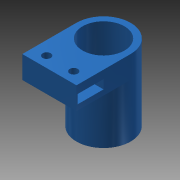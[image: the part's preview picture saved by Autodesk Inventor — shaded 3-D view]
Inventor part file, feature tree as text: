
AUTODESK INVENTOR PART (.ipt)
format: ipt  version: 2013 (Build 170138000, 138)  size: 145,920 bytes
history: native  units: mm
features: extrude x5, sketch x5, plane x2, projected_geometry x1
ambient origin geometry x8: Origin, YZ Plane, XZ Plane, XY Plane, X Axis, Y Axis, Z Axis, Center Point
bodies: Solid1 (feature_tree)
feature tree (13):
  extrude  "Extrusion1"  Depth=30.0mm
  extrude  "Extrusion2"  Depth=15.5mm
  sketch  "Sketch6"  dims[d9=10.0mm d10=5.0mm d11=5.0mm d12=25.0mm d13=0.0mm d15=2.0mm d16=0.0mm d18=3.0mm d19=0.0mm d20=10.0mm d21=0.4mm d22=0.2mm d23=0.0mm d25=3.3mm]
  plane  "Work Plane1"
  extrude  "Extrusion3"  Depth=3.0mm
  extrude  "Extrusion4"  Depth=4.0mm
  extrude  "Extrusion5"  Depth=5.0mm
  sketch  "Sketch1"  dims[d0=20.0mm d1=30.0mm]
  sketch  "Sketch2"  dims[d2=3.0mm d3=0.0mm d4=15.5mm]
  sketch  "Sketch3"  dims[d5=10.0mm d6=3.0mm]
  projected_geometry  "Projected Loop1"
  sketch  "Sketch5"  dims[d7=3.0mm d8=4.0mm]
  plane  "Work Plane2"
